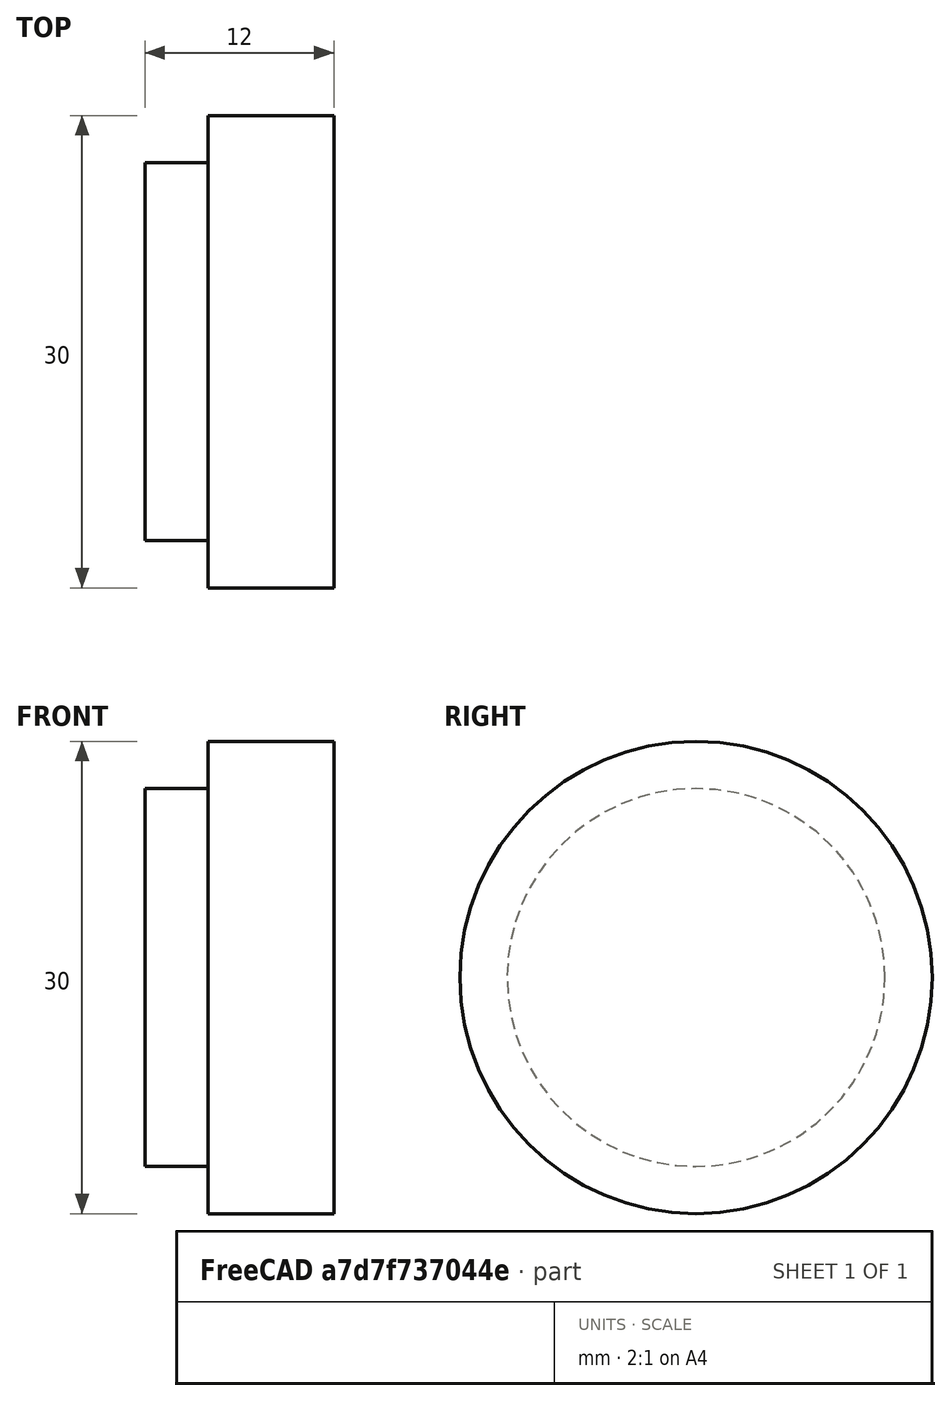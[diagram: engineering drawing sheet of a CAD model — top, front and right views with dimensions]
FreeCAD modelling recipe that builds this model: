
FCSTD DOCUMENT  (FreeCAD 0.19R)
Label: button
License: All rights reserved
LicenseURL: http://en.wikipedia.org/wiki/All_rights_reserved
objects: Sketcher::SketchObject×1, PartDesign::Revolution×1, PartDesign::Body×1
note: 4 computed .brp shape members not serialized (recipe doc carries the construction recipe); baked Part::Feature solids carry a one-line shape summary decoded from their .brp

FEATURE [Sketcher::SketchObject] Sketch
  MapMode = 5
  Support = -> [XY_Plane]
  sketch-geometry (6):
    g0: LineSegment StartX=0 StartY=0 StartZ=0 EndX=0 EndY=12 EndZ=0
    g1: LineSegment StartX=0 StartY=12 StartZ=0 EndX=4 EndY=12 EndZ=0
    g2: LineSegment StartX=4 StartY=12 StartZ=0 EndX=4 EndY=15 EndZ=0
    g3: LineSegment StartX=4 StartY=15 StartZ=0 EndX=12 EndY=15 EndZ=0
    g4: LineSegment StartX=12 StartY=15 StartZ=0 EndX=12 EndY=0 EndZ=0
    g5: LineSegment StartX=12 StartY=0 StartZ=0 EndX=0 EndY=0 EndZ=0
  constraints (17):
    c: Coincident(g0,g-1)
    c: Vertical(g0)
    c: Coincident(g1,g0)
    c: Horizontal(g1)
    c: Coincident(g2,g1)
    c: Vertical(g2)
    c: Coincident(g3,g2)
    c: Horizontal(g3)
    c: Coincident(g4,g3)
    c: PointOnObject(g4,g-1)
    c: Vertical(g4)
    c: Coincident(g5,g4)
    c: Coincident(g5,g0)
    c: Distance(g4,g3) = 15
    c: Distance(g2) = 3
    c: Distance(g4,g0) = 12
    c: Distance(g1) = 4
FEATURE [PartDesign::Revolution] Revolution
  AllowMultiFace = false
  Angle = 360
  Axis = (1,0,0)
  Base = (0,0,0)
  Profile = -> Sketch
  ReferenceAxis = -> X_Axis
FEATURE [PartDesign::Body] Body
  Group = -> [Sketch,Revolution]
  Origin = -> Origin
  Tip = -> Revolution
